# Revit family: Cim 746 PRF
name_source: partatom
category: Attrezzatura meccanica
revit_build: Autodesk Revit 2016 (Build: 20160126_1600(x64)
units: mm (PartAtom-declared; Revit-internal decimal feet)

## family parameters
Basato su piano di lavoro = No
Condiviso = Sì
Numero OmniClass = 23.75.00.00
Punto di calcolo locali = No
Quota connettore circolare = Usa diametro
Sempre verticale = Sì
Taglio con vuoti quando caricato = No
Tipo di parte = Normale
Titolo OmniClass = Climate Control (HVAC)

## types (6) — shared parameters
CR Brass = Brass
Descrizione = Combined manual presetting valve
Fluids = Water and Glycol
Max. flow temperature = 120°C
Max. static working pressure = 25   bar
Min. temperature = -10°C
Modello = Cim 746 PRF
Produttore = Cimberio
Technical Data Sheet = http://web.cimberio.it
URL = http://www.cimberio.it
s1 = 2 mm  [stored 0.00656168 ft]

## per-type parameters (varying)
- DN 15 1/2''x1/2'': CHa=24 mm; CHb=24 mm; Ca=3 mm  [stored 0.00984252 ft]; Cb=5 mm  [stored 0.0164042 ft]; Cc=12 mm  [stored 0.0393701 ft]; Cd=8 mm  [stored 0.0262467 ft]; Ce=18 mm  [stored 0.0590551 ft]; DN=15 mm  [stored 0.0492126 ft]; DN/2=8 mm  [stored 0.0262467 ft]; Hch=14 mm  [stored 0.0459318 ft]; Kv=0.47 - 2; Kvs=2.3; R1=8 mm  [stored 0.0262467 ft]; R2=9 mm  [stored 0.0295276 ft]; R3=10 mm  [stored 0.0328084 ft]; R4=12 mm  [stored 0.0393701 ft]; R5=13 mm; R6=10 mm  [stored 0.0328084 ft]; R7=10 mm  [stored 0.0328084 ft]; R8=9 mm  [stored 0.0295276 ft]; Sch=13 mm; Technical Code=DA04015015; Weight=470   Grms.; di=31 mm  [stored 0.101706 ft]; di1=41 mm  [stored 0.134514 ft]; di2=10 mm  [stored 0.0328084 ft]; dsa=37 mm  [stored 0.121391 ft]; dsb=37 mm  [stored 0.121391 ft]; h=26 mm; l=13 mm; s2=7 mm  [stored 0.0229659 ft]; s3=9 mm  [stored 0.0295276 ft]; s4=5 mm  [stored 0.0164042 ft]; s5=6 mm  [stored 0.019685 ft]; s6=2 mm  [stored 0.00656168 ft]
- DN 20 3/4''x3/4'': CHa=32 mm  [stored 0.104987 ft]; CHb=23 mm  [stored 0.0754593 ft]; Ca=5 mm  [stored 0.0164042 ft]; Cb=13 mm; Cc=4 mm  [stored 0.0131234 ft]; Cd=7 mm  [stored 0.0229659 ft]; Ce=24 mm; DN=20 mm  [stored 0.0656168 ft]; DN/2=10 mm  [stored 0.0328084 ft]; Hch=16 mm  [stored 0.0524934 ft]; Kv=0.54 - 3.88; Kvs=5.3; R1=10 mm  [stored 0.0328084 ft]; R2=12 mm  [stored 0.0393701 ft]; R3=11 mm  [stored 0.0360892 ft]; R4=13 mm; R5=17 mm; R6=14 mm  [stored 0.0459318 ft]; R7=13 mm; R8=13 mm; Sch=15 mm  [stored 0.0492126 ft]; Technical Code=DA04015022; Weight=585 Grms.; di=31 mm  [stored 0.101706 ft]; di1=41 mm  [stored 0.134514 ft]; di2=10 mm  [stored 0.0328084 ft]; dsa=47 mm; dsb=38 mm  [stored 0.124672 ft]; h=26 mm; l=14 mm  [stored 0.0459318 ft]; s2=11 mm  [stored 0.0360892 ft]; s3=7 mm  [stored 0.0229659 ft]; s4=7 mm  [stored 0.0229659 ft]; s5=7 mm  [stored 0.0229659 ft]; s6=1 mm  [stored 0.00328084 ft]
- DN 25 1"x1": CHa=42 mm  [stored 0.137795 ft]; CHb=25 mm  [stored 0.082021 ft]; Ca=5 mm  [stored 0.0164042 ft]; Cb=10 mm  [stored 0.0328084 ft]; Cc=4 mm  [stored 0.0131234 ft]; Cd=11 mm  [stored 0.0360892 ft]; Ce=34 mm; DN=25 mm  [stored 0.082021 ft]; DN/2=13 mm; Hch=20 mm  [stored 0.0656168 ft]; Kv=0.96 - 7.28; Kvs=9.2; R1=12 mm  [stored 0.0393701 ft]; R2=16 mm  [stored 0.0524934 ft]; R3=15 mm  [stored 0.0492126 ft]; R4=17 mm; R5=20 mm  [stored 0.0656168 ft]; R6=17 mm; R7=16 mm  [stored 0.0524934 ft]; R8=16 mm  [stored 0.0524934 ft]; Sch=16 mm  [stored 0.0524934 ft]; Technical Code=DA04015028; Weight=746 Grms.; di=35 mm  [stored 0.114829 ft]; di1=45 mm; di2=15 mm  [stored 0.0492126 ft]; dsa=58 mm; dsb=41 mm  [stored 0.134514 ft]; h=30 mm  [stored 0.0984252 ft]; l=16 mm  [stored 0.0524934 ft]; s2=5 mm  [stored 0.0164042 ft]; s3=8 mm  [stored 0.0262467 ft]; s4=7 mm  [stored 0.0229659 ft]; s5=7 mm  [stored 0.0229659 ft]; s6=4 mm  [stored 0.0131234 ft]
- DN 32 1.1/4"x1.1/4": CHa=50 mm; CHb=29 mm; Ca=10 mm  [stored 0.0328084 ft]; Cb=12 mm  [stored 0.0393701 ft]; Cc=14 mm  [stored 0.0459318 ft]; Cd=3 mm  [stored 0.00984252 ft]; Ce=37 mm  [stored 0.121391 ft]; DN=32 mm  [stored 0.104987 ft]; DN/2=16 mm  [stored 0.0524934 ft]; Hch=25 mm  [stored 0.082021 ft]; Kv=1.56 - 13.39; Kvs=19; R1=13 mm; R2=18 mm  [stored 0.0590551 ft]; R3=18 mm  [stored 0.0590551 ft]; R4=20 mm  [stored 0.0656168 ft]; R5=23 mm  [stored 0.0754593 ft]; R6=20 mm  [stored 0.0656168 ft]; R7=19 mm; R8=19 mm; Sch=20 mm  [stored 0.0656168 ft]; Technical Code=DA04015035; Weight=1196 Grms.; di=41 mm  [stored 0.134514 ft]; di1=51 mm; di2=15 mm  [stored 0.0492126 ft]; dsa=70 mm; dsb=49 mm; h=36 mm  [stored 0.11811 ft]; l=22 mm  [stored 0.0721785 ft]; s2=8 mm  [stored 0.0262467 ft]; s3=8 mm  [stored 0.0262467 ft]; s4=7 mm  [stored 0.0229659 ft]; s5=7 mm  [stored 0.0229659 ft]; s6=1 mm  [stored 0.00328084 ft]
- DN 40 1.1/2"x1.1/2": CHa=63 mm; CHb=41 mm  [stored 0.134514 ft]; Ca=10 mm  [stored 0.0328084 ft]; Cb=11 mm  [stored 0.0360892 ft]; Cc=28 mm  [stored 0.0918635 ft]; Cd=3 mm  [stored 0.00984252 ft]; Ce=50 mm; DN=40 mm  [stored 0.131234 ft]; DN/2=20 mm  [stored 0.0656168 ft]; Hch=30 mm  [stored 0.0984252 ft]; Kv=3.37 - 18.69; Kvs=22.1; R1=15 mm  [stored 0.0492126 ft]; R2=21 mm  [stored 0.0688976 ft]; R3=20 mm  [stored 0.0656168 ft]; R4=22 mm  [stored 0.0721785 ft]; R5=26 mm; R6=23 mm  [stored 0.0754593 ft]; R7=22 mm  [stored 0.0721785 ft]; R8=21 mm  [stored 0.0688976 ft]; Sch=20 mm  [stored 0.0656168 ft]; Technical Code=DA04015042; Weight=1744 Grms.; di=60 mm; di1=70 mm; di2=20 mm  [stored 0.0656168 ft]; dsa=83 mm; dsb=61 mm; h=55 mm; l=30 mm  [stored 0.0984252 ft]; s2=10 mm  [stored 0.0328084 ft]; s3=10 mm  [stored 0.0328084 ft]; s4=8 mm  [stored 0.0262467 ft]; s5=7 mm  [stored 0.0229659 ft]; s6=1 mm  [stored 0.00328084 ft]
- DN 50 2"x2": CHa=70 mm; CHb=43 mm  [stored 0.141076 ft]; Ca=11 mm  [stored 0.0360892 ft]; Cb=14 mm  [stored 0.0459318 ft]; Cc=26 mm; Cd=4 mm  [stored 0.0131234 ft]; Ce=56 mm; DN=50 mm; DN/2=25 mm  [stored 0.082021 ft]; Hch=35 mm  [stored 0.114829 ft]; Kv=4.39 - 30.10; Kvs=42.3; R1=15 mm  [stored 0.0492126 ft]; R2=21 mm  [stored 0.0688976 ft]; R3=23 mm  [stored 0.0754593 ft]; R4=25 mm  [stored 0.082021 ft]; R5=29 mm; R6=26 mm; R7=25 mm  [stored 0.082021 ft]; R8=25 mm  [stored 0.082021 ft]; Sch=25 mm  [stored 0.082021 ft]; Technical Code=DA04015054; Weight=2150 Grms.; di=60 mm; di1=70 mm; di2=20 mm  [stored 0.0656168 ft]; dsa=95 mm; dsb=68 mm; h=55 mm; l=30 mm  [stored 0.0984252 ft]; s2=10 mm  [stored 0.0328084 ft]; s3=10 mm  [stored 0.0328084 ft]; s4=7 mm  [stored 0.0229659 ft]; s5=7 mm  [stored 0.0229659 ft]; s6=1 mm  [stored 0.00328084 ft]

note: [stored X ft] marks values corroborated as IEEE doubles in the binary element streams (Revit-internal decimal feet)

## geometry (parser evidence)
native form markers: Sweep x11
no freeform markers — native parametric forms only
